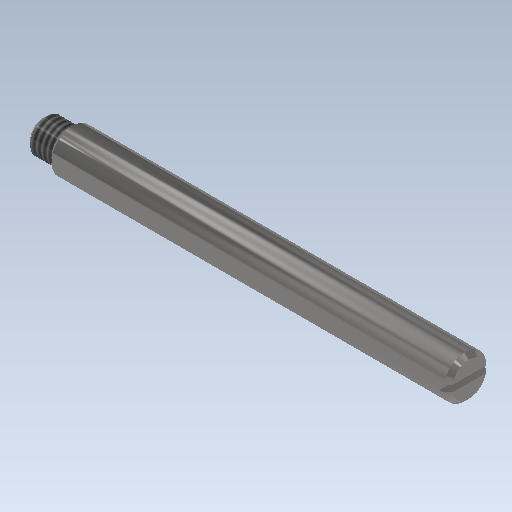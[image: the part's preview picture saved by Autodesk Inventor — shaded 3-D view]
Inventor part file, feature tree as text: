
AUTODESK INVENTOR PART (.ipt)
format: ipt  version: 2020.1 (Build 241239000, 239)  size: 136,704 bytes
history: native  units: mm
features: chamfer x2, sketch x2, revolve x1, thread x1, extrude x1
ambient origin geometry x8: Origin, YZ Plane, XZ Plane, XY Plane, X Axis, Y Axis, Z Axis, Center Point
bodies: Solid1 (feature_tree)
feature tree (7):
  revolve  "Revolution1"  [1 undecoded]
  thread  "Thread1"  [1 undecoded]
  chamfer  "Chamfer1"  Distance=10.0mm
  extrude  "Extrusion1"  Depth=10.0mm TaperAngle=45.0deg
  chamfer  "Chamfer2"  Distance=1.5mm
  sketch  "Sketch1"  dims[d0=8.0mm d1=10.0mm d3=100.0mm]
  sketch  "Sketch2"  dims[d4=90.0deg d5=10.0mm d6=0.0mm d7=1.0mm d8=2.0mm d9=45.0deg d10=1.5mm d11=2.0mm d12=10.0mm d13=0.0mm d14=1.0mm d15=2.0mm d16=45.0deg d17=7.0mm d18=1.0mm d19=7.0mm]
note: 2 required parameter values undecoded (feature->parameter linkage not recoverable at this tier; creation-order binding heuristic only, values carry confidence <= 0.55)